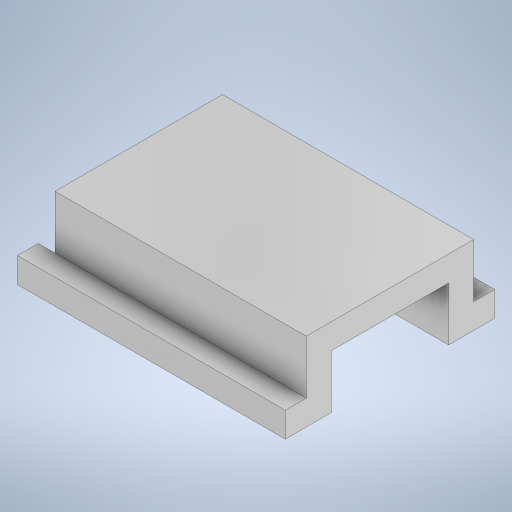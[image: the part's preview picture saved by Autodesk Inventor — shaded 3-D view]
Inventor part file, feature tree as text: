
AUTODESK INVENTOR PART (.ipt)
format: ipt  version: 2024 (Build 280153000, 153)  size: 248,832 bytes
history: native  units: mm
features: extrude x3, sketch x3
ambient origin geometry x8: Origin, YZ Plane, XZ Plane, XY Plane, X Axis, Y Axis, Z Axis, Center Point
bodies: Solid1 (feature_tree)
feature tree (6):
  extrude  "Extrusion1"  Depth=150.0mm
  extrude  "Extrusion2"  Depth=15.0mm
  extrude  "Extrusion3"  Depth=15.0mm
  sketch  "Sketch1"  dims[d0=100.0mm d1=150.0mm]
  sketch  "Sketch2"  dims[d2=47.0mm d3=0.0mm d4=15.0mm]
  sketch  "Sketch3"  dims[d5=15.0mm d6=15.0mm d7=200.0mm d8=0.0mm d9=12.5mm d10=12.5mm d11=15.0mm d12=15.0mm d13=160.0mm d14=0.0mm]
